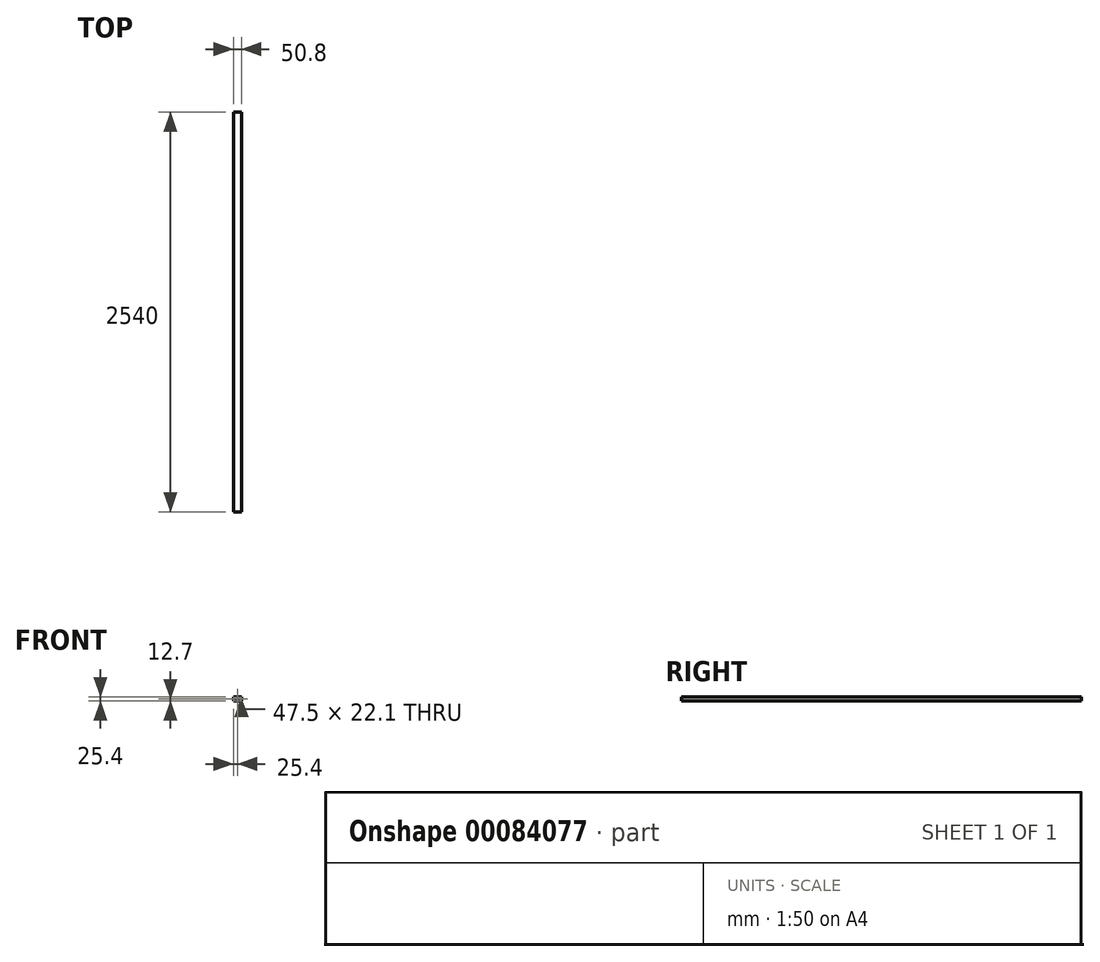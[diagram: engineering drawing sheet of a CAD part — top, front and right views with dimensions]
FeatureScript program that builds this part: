
annotation { "Feature Type Name" : "Feature", "Feature Type Description" : "" }
export const myFeature = defineFeature(function(context is Context, id is Id, definition is map)
    precondition{}
    {
        {
            var Q0;
            Q0=qCreatedBy(makeId("Front.planeOp"),FACE);
            var sketch = newSketch(context, id + "F0", { "sketchPlane" : qUnion([Q0])});
            skLineSegment(sketch, "E0.rect.bottom", {"start": v(25.4, -12.7) * mm, "end": v(-25.4, -12.7) * mm});
            skLineSegment(sketch, "E0.rect.top", {"start": v(25.4, 12.7) * mm, "end": v(-25.4, 12.7) * mm});
            skLineSegment(sketch, "E0.rect.left", {"start": v(25.4, -12.7) * mm, "end": v(25.4, 12.7) * mm});
            skLineSegment(sketch, "E0.rect.right", {"start": v(-25.4, -12.7) * mm, "end": v(-25.4, 12.7) * mm});
            skPoint(sketch, "E0.rect.middle", {"position": v(0, 0) * mm});
            skLineSegment(sketch, "E1.rect.bottom", {"start": v(23.75, -11.05) * mm, "end": v(-23.75, -11.05) * mm});
            skLineSegment(sketch, "E1.rect.top", {"start": v(23.75, 11.05) * mm, "end": v(-23.75, 11.05) * mm});
            skLineSegment(sketch, "E1.rect.left", {"start": v(23.75, -11.05) * mm, "end": v(23.75, 11.05) * mm});
            skLineSegment(sketch, "E1.rect.right", {"start": v(-23.75, -11.05) * mm, "end": v(-23.75, 11.05) * mm});
            skSolve(sketch);
        }
        {
            var Q0;
            Q0=makeQuery(id+"F0.imprint","IMPRINT",FACE,{"disambiguationData":[TD([[makeQuery(id+"F0.imprint","IMPRINT",EDGE,{"derivedFrom":sQuery(id+"F0.wireOp",EDGE,"E0.rect.bottom")}),-1.0]])]});
            extrude(context, id + "F1", {"entities" : qUnion([Q0]), "oppositeDirection" : true, "depth" : 2540 * mm});
        }
        {
            var Q0;
            Q0=makeQuery(id+"F1.opExtrude","SWEPT_FACE",FACE,{"disambiguationData":[OSD([sQuery(id+"F0.wireOp",EDGE,"E0.rect.top")])]});
            var sketch = newSketch(context, id + "F2", { "sketchPlane" : qUnion([Q0])});
            skPoint(sketch, "E2", {"position": v(0, 1638.3) * mm});
            skPoint(sketch, "E3", {"position": v(0, 825.5) * mm});
            skPoint(sketch, "E4", {"position": v(0, 419.1) * mm});
            skPoint(sketch, "E5", {"position": v(0, 1231.9) * mm});
            skSolve(sketch);
        }
    });
